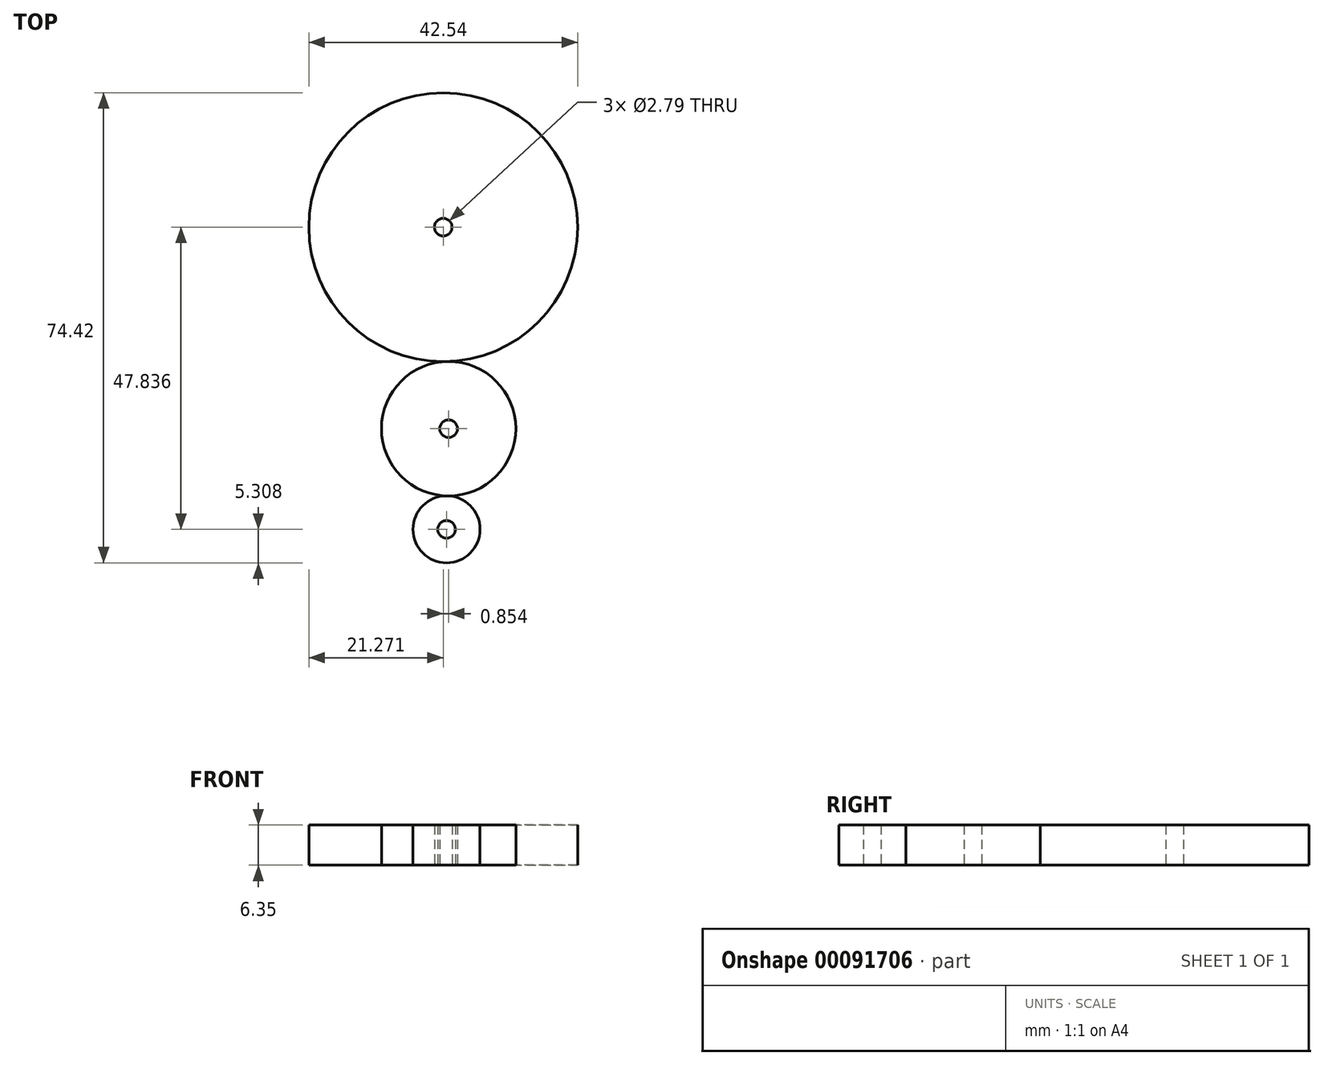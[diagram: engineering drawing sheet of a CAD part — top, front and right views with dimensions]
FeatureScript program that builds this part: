
annotation { "Feature Type Name" : "Feature", "Feature Type Description" : "" }
export const myFeature = defineFeature(function(context is Context, id is Id, definition is map)
    precondition{}
    {
        {
            var Q0;
            Q0=qCreatedBy(makeId("Top.planeOp"),FACE);
            var sketch = newSketch(context, id + "F0", { "sketchPlane" : qUnion([Q0])});
            skCircle(sketch, "E0", {"center": v(-21.86, 46.77) * mm, "radius": 21.27 * mm});
            skCircle(sketch, "E1", {"center": v(-21, 14.88) * mm, "radius": 10.64 * mm});
            skCircle(sketch, "E2", {"center": v(-21.33, -1.06) * mm, "radius": 5.3 * mm});
            skLineSegment(sketch, "E3", {"start": v(-23.84, 79.41) * mm, "end": v(-54.77, 71.34) * mm});
            skLineSegment(sketch, "E4", {"start": v(-54.77, 71.34) * mm, "end": v(-54.77, 9.97) * mm});
            skLineSegment(sketch, "E5", {"start": v(-54.77, 9.97) * mm, "end": v(-20.08, -40.23) * mm});
            skLineSegment(sketch, "E6", {"start": v(-20.08, -40.23) * mm, "end": v(10.04, 9.37) * mm});
            skLineSegment(sketch, "E7", {"start": v(10.04, 9.37) * mm, "end": v(10.04, 70.65) * mm});
            skLineSegment(sketch, "E8", {"start": v(10.04, 70.65) * mm, "end": v(-23.84, 79.41) * mm});
            skCircle(sketch, "E9", {"center": v(-21.86, 46.77) * mm, "radius": 1.4 * mm});
            skCircle(sketch, "E10", {"center": v(-21, 14.88) * mm, "radius": 1.4 * mm});
            skCircle(sketch, "E11", {"center": v(-21.33, -1.06) * mm, "radius": 1.4 * mm});
            skSolve(sketch);
        }
        {
            var Q0;
            Q0=qCreatedBy(makeId("Top.planeOp"),FACE);
            var sketch = newSketch(context, id + "F1", { "sketchPlane" : qUnion([Q0])});
            skLineSegment(sketch, "E12.bottom", {"start": v(112.45, -108.39) * mm, "end": v(-103.45, -108.39) * mm});
            skLineSegment(sketch, "E12.top", {"start": v(112.45, 171.01) * mm, "end": v(-103.45, 171.01) * mm});
            skLineSegment(sketch, "E12.left", {"start": v(112.45, -108.39) * mm, "end": v(112.45, 171.01) * mm});
            skLineSegment(sketch, "E12.right", {"start": v(-103.45, -108.39) * mm, "end": v(-103.45, 171.01) * mm});
            skSolve(sketch);
        }
        {
            var Q0;
            Q0=sQuery(id+"F0.wireOp",EDGE,"E0");
            extrude(context, id + "F2", {"bodyType" : ToolBodyType.SURFACE, "surfaceEntities" : qUnion([Q0]), "depth" : 6.35 * mm});
        }
        {
            var Q0;
            Q0=sQuery(id+"F0.wireOp",EDGE,"E1");
            extrude(context, id + "F3", {"bodyType" : ToolBodyType.SURFACE, "surfaceEntities" : qUnion([Q0]), "depth" : 6.35 * mm});
        }
        {
            var Q0;
            Q0=sQuery(id+"F0.wireOp",EDGE,"E2");
            extrude(context, id + "F4", {"bodyType" : ToolBodyType.SURFACE, "surfaceEntities" : qUnion([Q0]), "depth" : 6.35 * mm});
        }
        {
            var Q0;
            Q0=makeQuery(id+"F0.imprint","IMPRINT",FACE,{"disambiguationData":[TD([[makeQuery(id+"F0.imprint","IMPRINT",EDGE,{"derivedFrom":sQuery(id+"F0.wireOp",EDGE,"E0")}),1.0]])]});
            extrude(context, id + "F5", {"entities" : qUnion([Q0]), "depth" : 6.35 * mm});
        }
        {
            var Q0;
            Q0=makeQuery(id+"F0.imprint","IMPRINT",FACE,{"disambiguationData":[TD([[makeQuery(id+"F0.imprint","IMPRINT",EDGE,{"derivedFrom":sQuery(id+"F0.wireOp",EDGE,"E10")}),-1.0]])]});
            extrude(context, id + "F6", {"entities" : qUnion([Q0]), "operationType" : NewBodyOperationType.ADD, "depth" : 6.35 * mm});
        }
        {
            var Q0;
            Q0=makeQuery(id+"F0.imprint","IMPRINT",FACE,{"disambiguationData":[TD([[makeQuery(id+"F0.imprint","IMPRINT",EDGE,{"derivedFrom":sQuery(id+"F0.wireOp",EDGE,"E2")}),1.0]])]});
            extrude(context, id + "F7", {"entities" : qUnion([Q0]), "operationType" : NewBodyOperationType.ADD, "depth" : 6.35 * mm});
        }
        {
            var Q0;
            Q0=makeQuery(id+"F1.imprint","IMPRINT",FACE,{"disambiguationData":[TD([[makeQuery(id+"F1.imprint","IMPRINT",EDGE,{"derivedFrom":sQuery(id+"F1.wireOp",EDGE,"E12.bottom")}),-1.0]])]});
            var sketch = newSketch(context, id + "F8", { "sketchPlane" : qUnion([Q0])});
            skCircle(sketch, "E13", {"center": v(-65.74, -4.73) * mm, "radius": 1.4 * mm});
            skSolve(sketch);
        }
        {
            var Q0;
            Q0=sQuery(id+"F8.wireOp",EDGE,"E13");
            extrude(context, id + "F9", {"bodyType" : ToolBodyType.SURFACE, "surfaceEntities" : qUnion([Q0]), "depth" : 76.2 * mm});
        }
        {
            var Q0;
            Q0=makeQuery(id+"F1.imprint","IMPRINT",FACE,{"disambiguationData":[TD([[makeQuery(id+"F1.imprint","IMPRINT",EDGE,{"derivedFrom":sQuery(id+"F1.wireOp",EDGE,"E12.bottom")}),-1.0]])]});
            var sketch = newSketch(context, id + "F10", { "sketchPlane" : qUnion([Q0])});
            skCircle(sketch, "E14", {"center": v(-70.96, 20.74) * mm, "radius": 1.4 * mm});
            skSolve(sketch);
        }
        {
            var Q0;
            Q0=makeQuery(id+"F1.imprint","IMPRINT",FACE,{"disambiguationData":[TD([[makeQuery(id+"F1.imprint","IMPRINT",EDGE,{"derivedFrom":sQuery(id+"F1.wireOp",EDGE,"E12.bottom")}),-1.0]])]});
            var sketch = newSketch(context, id + "F11", { "sketchPlane" : qUnion([Q0])});
            skCircle(sketch, "E15", {"center": v(-70.8, 35.45) * mm, "radius": 1.4 * mm});
            skSolve(sketch);
        }
        {
            var Q0;
            Q0=sQuery(id+"F11.wireOp",EDGE,"E15");
            extrude(context, id + "F12", {"bodyType" : ToolBodyType.SURFACE, "surfaceEntities" : qUnion([Q0]), "depth" : 76.2 * mm});
        }
        {
            var Q0;
            Q0=sQuery(id+"F10.wireOp",EDGE,"E14");
            extrude(context, id + "F13", {"bodyType" : ToolBodyType.SURFACE, "surfaceEntities" : qUnion([Q0]), "depth" : 76.2 * mm});
        }
    });
